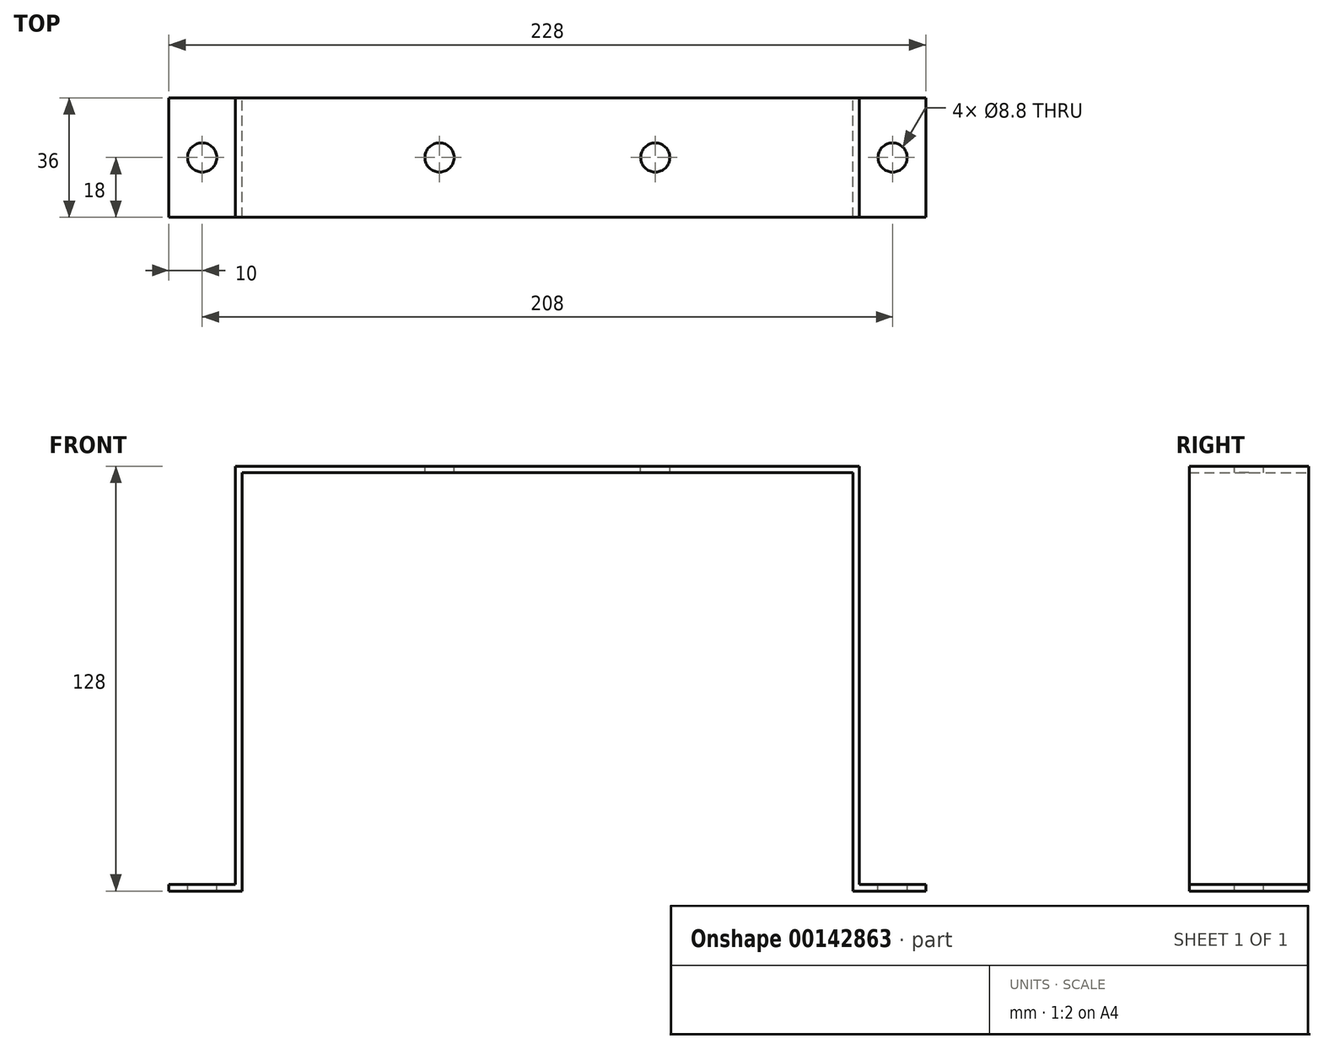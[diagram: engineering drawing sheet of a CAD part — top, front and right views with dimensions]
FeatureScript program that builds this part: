
annotation { "Feature Type Name" : "Feature", "Feature Type Description" : "" }
export const myFeature = defineFeature(function(context is Context, id is Id, definition is map)
    precondition{}
    {
        {
            var Q0;
            Q0=qCreatedBy(makeId("Front.planeOp"),FACE);
            var sketch = newSketch(context, id + "F0", { "sketchPlane" : qUnion([Q0])});
            skLineSegment(sketch, "E0.bottom", {"start": v(94, 63) * mm, "end": v(-94, 63) * mm});
            skLineSegment(sketch, "E0.left", {"start": v(94, 63) * mm, "end": v(94, -63) * mm});
            skLineSegment(sketch, "E0.right", {"start": v(-94, 63) * mm, "end": v(-94, -63) * mm});
            skPoint(sketch, "E0.middle", {"position": v(0, 0) * mm});
            skLineSegment(sketch, "E1", {"start": v(-94, -63) * mm, "end": v(-114, -63) * mm});
            skLineSegment(sketch, "E2.MirrorCS", {"start": v(94, -63) * mm, "end": v(114, -63) * mm});
            skLineSegment(sketch, "E3.0", {"start": v(-92, -65) * mm, "end": v(-114, -65) * mm});
            skLineSegment(sketch, "E3.1", {"start": v(92, -65) * mm, "end": v(114, -65) * mm});
            skLineSegment(sketch, "E3.2", {"start": v(92, 61) * mm, "end": v(92, -65) * mm});
            skLineSegment(sketch, "E3.3", {"start": v(92, 61) * mm, "end": v(-92, 61) * mm});
            skLineSegment(sketch, "E3.4", {"start": v(-92, 61) * mm, "end": v(-92, -65) * mm});
            skLineSegment(sketch, "E4", {"start": v(-114, -63) * mm, "end": v(-114, -65) * mm});
            skLineSegment(sketch, "E5", {"start": v(114, -63) * mm, "end": v(114, -65) * mm});
            skSolve(sketch);
        }
        {
            var Q0;
            Q0=makeQuery(id+"F0.imprint","IMPRINT",FACE,{"disambiguationData":[TD([[makeQuery(id+"F0.imprint","IMPRINT",EDGE,{"derivedFrom":sQuery(id+"F0.wireOp",EDGE,"E0.bottom")}),1.0]])]});
            extrude(context, id + "F1", {"entities" : qUnion([Q0]), "endBound" : BoundingType.SYMMETRIC, "depth" : 36 * mm});
        }
        {
            var Q0;
            Q0=makeQuery(id+"F1.opExtrude","SWEPT_FACE",FACE,{"disambiguationData":[OSD([sQuery(id+"F0.wireOp",EDGE,"E0.bottom")])]});
            var sketch = newSketch(context, id + "F2", { "sketchPlane" : qUnion([Q0])});
            skPoint(sketch, "E6", {"position": v(0, 0) * mm});
            skPoint(sketch, "E7", {"position": v(32.5, 0) * mm});
            skPoint(sketch, "E8.MirrorP", {"position": v(-32.5, 0) * mm});
            skSolve(sketch);
        }
        {
            var Q0;
            Q0=makeQuery(id+"F1.opExtrude","SWEPT_FACE",FACE,{"disambiguationData":[OSD([sQuery(id+"F0.wireOp",EDGE,"E1")])]});
            var sketch = newSketch(context, id + "F3", { "sketchPlane" : qUnion([Q0])});
            skPoint(sketch, "E9", {"position": v(-104, 0) * mm});
            skPoint(sketch, "E9.positionSnap0", {"position": v(-104, 18) * mm});
            skPoint(sketch, "E9.positionSnap1", {"position": v(-114, 0) * mm});
            skSolve(sketch);
        }
        {
            var Q0;
            Q0=makeQuery(id+"F1.opExtrude","SWEPT_FACE",FACE,{"disambiguationData":[OSD([sQuery(id+"F0.wireOp",EDGE,"E2.MirrorCS")])]});
            var sketch = newSketch(context, id + "F4", { "sketchPlane" : qUnion([Q0])});
            skPoint(sketch, "E10", {"position": v(104, 0) * mm});
            skPoint(sketch, "E10.positionSnap0", {"position": v(114, 0) * mm});
            skPoint(sketch, "E10.positionSnap1", {"position": v(104, 18) * mm});
            skSolve(sketch);
        }
        {
            var Q0;
            Q0=sQuery(id+"F2.wireOp",VERTEX,"E8.MirrorP");
            var Q1;
            Q1=sQuery(id+"F2.wireOp",VERTEX,"E7");
            var Q2;
            Q2=sQuery(id+"F4.wireOp",VERTEX,"E10");
            var Q3;
            Q3=sQuery(id+"F3.wireOp",VERTEX,"E9");
            var Q4;
            Q4=makeQuery(id+"F1.opExtrude","SWEPT_BODY",BODY,{"disambiguationData":[OSD([sQuery(id+"F0.wireOp",EDGE,"E0.bottom"),sQuery(id+"F0.wireOp",EDGE,"E0.left"),sQuery(id+"F0.wireOp",EDGE,"E0.right"),sQuery(id+"F0.wireOp",EDGE,"E1"),sQuery(id+"F0.wireOp",EDGE,"E2.MirrorCS"),sQuery(id+"F0.wireOp",EDGE,"E3.0"),sQuery(id+"F0.wireOp",EDGE,"E3.1"),sQuery(id+"F0.wireOp",EDGE,"E3.2"),sQuery(id+"F0.wireOp",EDGE,"E3.3"),sQuery(id+"F0.wireOp",EDGE,"E3.4"),sQuery(id+"F0.wireOp",EDGE,"E4"),sQuery(id+"F0.wireOp",EDGE,"E5")])]});
            hole(context, id + "F5", {"style" : HoleStyle.SIMPLE, "endStyle" : HoleEndStyle.THROUGH, "standardTappedOrClearance" : lookupTablePath({ "standard" : "ISO", "fit" : "Normal", "size" : "M8", "type" : "Clearance" }), "standardBlindInLast" : lookupTablePath({ "fit" : "Standard", "standard" : "ISO", "size" : "M8", "type" : "Clearance" }), "holeDiameter" : 8.8 * mm, "locations" : qUnion([Q0, Q1, Q2, Q3]), "scope" : qUnion([Q4]), "isTappedThrough" : true});
        }
    });
